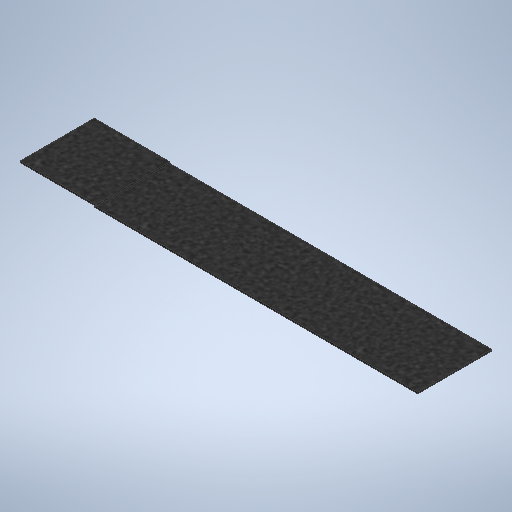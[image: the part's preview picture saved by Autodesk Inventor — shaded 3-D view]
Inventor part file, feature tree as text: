
AUTODESK INVENTOR PART (.ipt)
format: ipt  version: 2025 (Build 290162010, 162A)  size: 281,600 bytes
history: native  units: in
note: dims shown in document units (in); Inventor stores cm internally (conversion verified against a paired STEP export)
features: extrude x1, sketch x1
ambient origin geometry x8: Origin, YZ Plane, XZ Plane, XY Plane, X Axis, Y Axis, Z Axis, Center Point
bodies: Body1 (feature_tree)
feature tree (2):
  extrude  "Extrusion2"  Depth=0.125in
  sketch  "Sketch1"  dims[d0=6.5in d1=0.125in d2=0.125in d3=0.125in d4=0.125in d8=6.5in d9=0.0in d10=28.375in]
